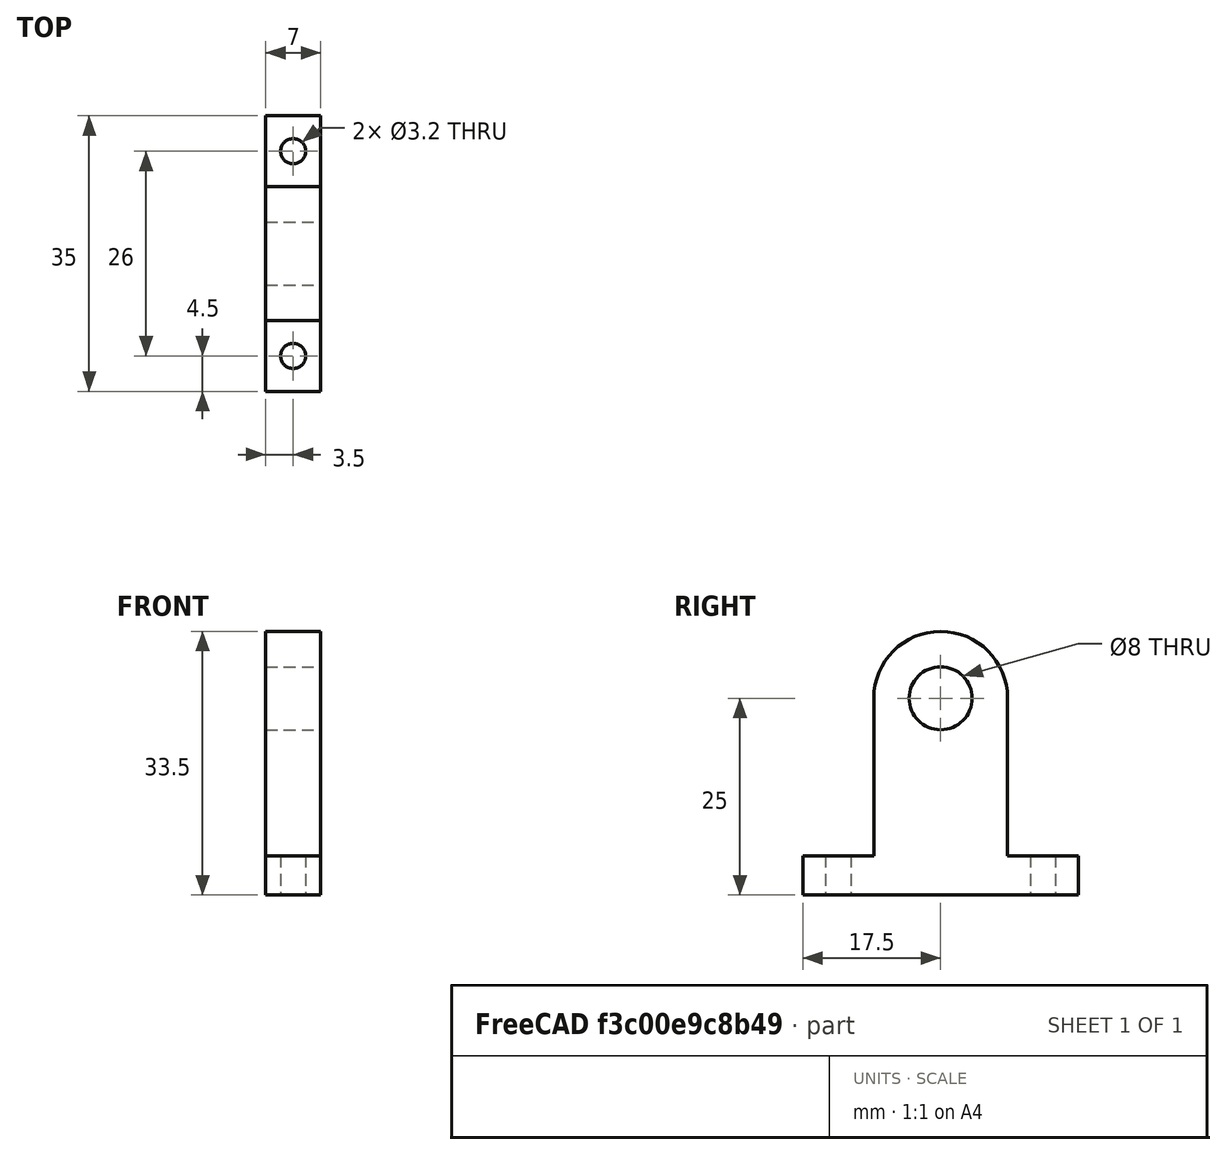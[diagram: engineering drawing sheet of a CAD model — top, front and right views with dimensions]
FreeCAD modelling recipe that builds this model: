
FCSTD DOCUMENT  (FreeCAD 0.18R16110 (Git))
Label: tube-mount-8mm-2x
License: All rights reserved
LicenseURL: http://en.wikipedia.org/wiki/All_rights_reserved
objects: Part::Cylinder×4, Part::Cut×3, Part::Box×2, Part::MultiFuse×1, Mesh::Feature×1
note: 10 computed .brp shape members not serialized (recipe doc carries the construction recipe); baked Part::Feature solids carry a one-line shape summary decoded from their .brp

FEATURE [Part::Cylinder] Cylinder120  label="Zylinder093"
  Angle = 180
  AttacherType = Attacher::AttachEngine3D
  Height = 7
  Radius = 8.5
FEATURE [Part::Cylinder] Cylinder124  label="Zylinder097"
  Angle = 360
  AttacherType = Attacher::AttachEngine3D
  Height = 10
  Placement = pos=(13,-18,3.5) rot=(1,0,0;1.5708rad)
  Radius = 1.6
FEATURE [Part::Cylinder] Cylinder119  label="Zylinder092"
  Angle = 360
  AttacherType = Attacher::AttachEngine3D
  Height = 7
  Radius = 4
FEATURE [Part::Box] Box045  label="Quader039"
  AttacherType = Attacher::AttachEngine3D
  Height = 7
  Length = 17
  Placement = pos=(-8.5,-20,0) rot=(0,0,1;0rad)
  Width = 20
FEATURE [Part::Box] Box046  label="Quader040"
  AttacherType = Attacher::AttachEngine3D
  Height = 7
  Length = 35
  Placement = pos=(-17.5,-25,0) rot=(0,0,1;0rad)
  Width = 5
FEATURE [Part::MultiFuse] Fusion021
  Shapes = -> [Box046,Cylinder120,Box045]
FEATURE [Part::Cut] Cut151  label="Absaughalterung"
  Base = -> Fusion021
  Tool = -> Cylinder119
FEATURE [Part::Cut] Cut156
  Base = -> Cut151
  Tool = -> Cylinder124
FEATURE [Part::Cylinder] Cylinder132  label="Zylinder104"
  Angle = 360
  AttacherType = Attacher::AttachEngine3D
  Height = 10
  Placement = pos=(-13,-18,3.5) rot=(1,0,0;1.5708rad)
  Radius = 1.6
FEATURE [Part::Cut] Cut157  label="tube-mount-8mm-2x"
  Base = -> Cut156
  Placement = pos=(-92,79,-7) rot=(0.57735,0.57735,0.57735;2.0944rad)
  Tool = -> Cylinder132
FEATURE [Mesh::Feature] Mesh  label="tube-mount-8mm-2x (Meshed)"
